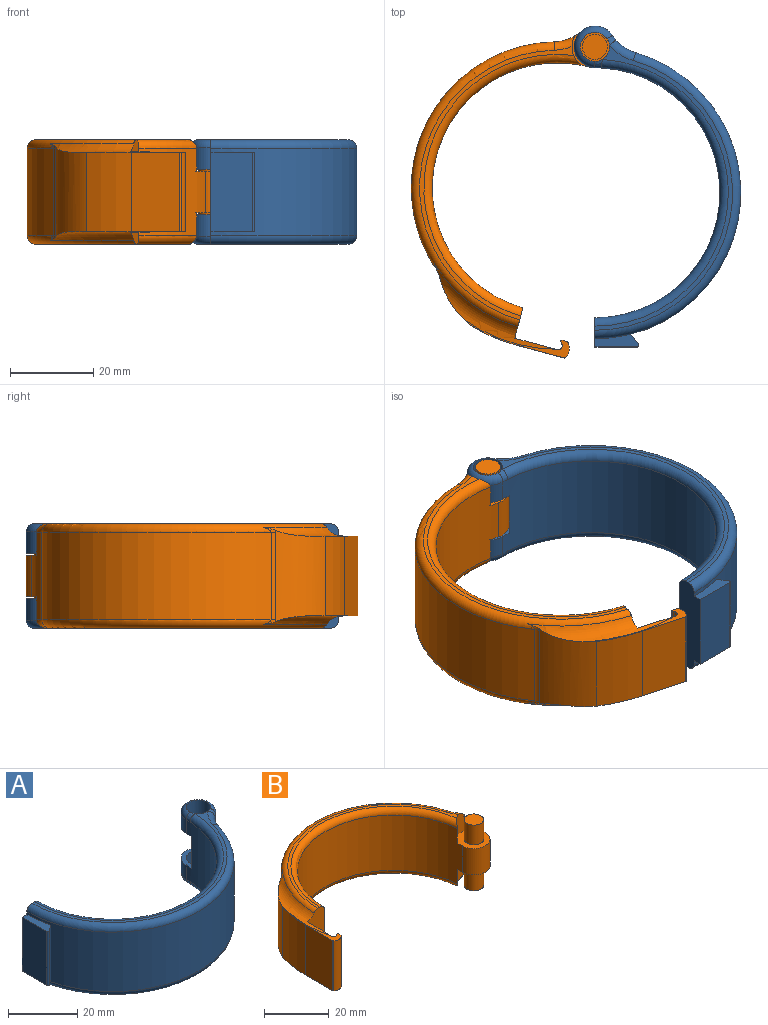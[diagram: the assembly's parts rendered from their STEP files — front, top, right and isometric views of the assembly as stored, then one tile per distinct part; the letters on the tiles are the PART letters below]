
ASSEMBLY  parts=2 mates=1
PART A: 30 faces, bbox 78.3x43.3x25.4 mm
  f0: cylinder r=35mm len=68.61mm, axis (0,0,-1), area 1936mm2, adj f4,f12,f13,f22,f27,f28,f29
  f1: cylinder r=3.5mm len=7mm, axis (0,0,-1), area 153.9mm2, adj f5,f11,f15,f16,f17
  f2: cylinder r=5mm len=10mm, axis (0,0,-1), area 104.6mm2, adj f3,f11,f12,f16
  f3: cylinder r=30mm len=60mm, axis (0,0,-1), area 1956mm2, adj f2,f4,f8,f9,f10,f11,f17,f18
  f4: plane 25x7mm, normal (0,1,0), area 159.6mm2, adj f0,f3,f5,f6,f13,f18,f19,f22
  f5: plane 68.36x33mm, normal (0,0,-1), area 104.8mm2, adj f1,f4,f13,f14,f18
  f6: plane 68.36x33mm, normal (0,0,1), area 104.8mm2, adj f4,f7,f19,f22,f24
  f7: cylinder r=3.5mm len=7mm, axis (0,0,-1), area 153.9mm2, adj f6,f10,f20,f21,f23
  f8: cylinder r=5mm len=10mm, axis (0,0,-1), area 104.6mm2, adj f3,f10,f12,f21
  f9: cylinder r=5.5mm len=11mm, axis (0,0,-1), area 85.3mm2, adj f3,f10,f11,f12
  f10: plane 10.5x10.08mm, normal (0,0,-1), area 44.4mm2, adj f3,f7,f8,f9,f12
  f11: plane 10.5x10.08mm, normal (0,0,1), area 44.4mm2, adj f1,f2,f3,f9,f12
  f12: cylinder r=10mm len=21.13mm, axis (0,0,1), area 128.3mm2, adj f0,f2,f8,f9,f10,f11,f14,f15
  f13: torus R=33mm, axis (0,0,1), area 307.8mm2, adj f0,f4,f5,f14
  f14: torus R=12mm, axis (0,0,1), area 19.3mm2, adj f5,f12,f13,f15
  f15: bspline ~2.98x2.54mm, area 4mm2, adj f1,f12,f14,f16
  f16: torus R=3mm, axis (0,0,-1), area 48.7mm2, adj f1,f2,f15,f17
  f17: bspline ~2.48x2.22mm, area 4.6mm2, adj f1,f3,f16,f18
  f18: torus R=32mm, axis (0,0,1), area 298.1mm2, adj f3,f4,f5,f17
  f19: torus R=32mm, axis (0,0,1), area 298.1mm2, adj f3,f4,f6,f20
  f20: bspline ~2.48x2.22mm, area 4.6mm2, adj f3,f7,f19,f21
  f21: torus R=3mm, axis (0,0,1), area 48.7mm2, adj f7,f8,f20,f23
  f22: torus R=33mm, axis (0,0,1), area 307.8mm2, adj f0,f4,f6,f24
  f23: bspline ~2.98x2.54mm, area 4mm2, adj f7,f12,f21,f24
  f24: torus R=12mm, axis (0,0,1), area 19.3mm2, adj f6,f12,f22,f23
  f25: plane 19x10mm, normal (-1,0,0), area 190mm2, adj f4,f26,f28,f29
  f26: cylinder r=0.5mm len=19mm, axis (0,0,-1), area 21.2mm2, adj f25,f27,f28,f29
  f27: plane 19x2.27mm, normal (0.62,-0.79,0), area 54.8mm2, adj f0,f26,f28,f29
  f28: plane 10.5x3.08mm, normal (0,0,1), area 23.8mm2, adj f0,f4,f25,f26,f27
  f29: plane 10.5x3.08mm, normal (0,0,-1), area 23.8mm2, adj f0,f4,f25,f26,f27
PART B: 41 faces, bbox 85.8x50.8x29 mm
  f0: cylinder r=35mm len=60.33mm, axis (0,0,-1), area 1585.1mm2, adj f14,f15,f17,f39
  f1: cylinder r=30mm len=60mm, axis (0,0,-1), area 1945.4mm2, adj f2,f3,f4,f7,f8,f11,f19,f20
  f2: plane 10.5x10.08mm, normal (0,0,1), area 54.6mm2, adj f1,f4,f9,f11,f14
  f3: plane 10.5x10.08mm, normal (0,0,-1), area 54.6mm2, adj f1,f7,f11,f13,f14
  f4: cylinder r=5.5mm len=7.5mm, axis (0,0,-1), area 52.5mm2, adj f1,f2,f5,f14,f16,f20
  f5: plane 66.63x32.5mm, normal (0,0,1), area 98.4mm2, adj f4,f8,f15,f16,f20
  f6: plane 66.63x32.5mm, normal (0,0,-1), area 98.4mm2, adj f7,f8,f17,f18,f19
  f7: cylinder r=5.5mm len=7.5mm, axis (0,0,-1), area 52.5mm2, adj f1,f3,f6,f14,f18,f19
  f8: plane 25.02x7.52mm, normal (0,-1,0), area 173mm2, adj f1,f5,f6,f15,f17,f19,f20,f30
  f9: cylinder r=3mm len=7.5mm, axis (0,0,-1), area 141.4mm2, adj f2,f10
  f10: plane 6x6mm, normal (0,0,1), area 28.3mm2, adj f9
  f11: cylinder r=5mm len=10mm, axis (0,0,-1), area 206.6mm2, adj f1,f2,f3,f14
  f12: plane 6x6mm, normal (0,0,-1), area 28.3mm2, adj f13
  f13: cylinder r=3mm len=7.5mm, axis (0,0,-1), area 141.4mm2, adj f3,f12
  f14: cylinder r=10mm len=21mm, axis (0,0,1), area 128.2mm2, adj f0,f2,f3,f4,f7,f11,f16,f18
  f15: torus R=33mm, axis (0,0,1), area 275.9mm2, adj f0,f5,f8,f16,f37,f40
  f16: torus R=12mm, axis (0,0,1), area 14.8mm2, adj f4,f5,f14,f15
  f17: torus R=33mm, axis (0,0,1), area 275.9mm2, adj f0,f6,f8,f18,f36,f38
  f18: torus R=12mm, axis (0,0,1), area 14.8mm2, adj f6,f7,f14,f17
  f19: torus R=32mm, axis (0,0,1), area 291.6mm2, adj f1,f6,f7,f8
  f20: torus R=32mm, axis (0,0,1), area 291.6mm2, adj f1,f4,f5,f8
  f21: cylinder r=0.35mm len=19mm, axis (0,0,-1), area 6.6mm2, adj f22,f33,f34,f35
  f22: plane 19x0.03mm, normal (-0.54,-0.84,0), area 0.7mm2, adj f21,f23,f34,f35
  f23: cylinder r=3.02mm len=19mm, axis (0,0,-1), area 71.2mm2, adj f22,f24,f34,f35
  f24: plane 19x0.12mm, normal (0.62,-0.79,0), area 2.8mm2, adj f23,f25,f34,f35
  f25: cylinder r=0.49mm len=19mm, axis (0,0,-1), area 8.4mm2, adj f24,f26,f34,f35
  f26: plane 19x1.19mm, normal (1,0,0), area 22.6mm2, adj f25,f27,f34,f35
  f27: cylinder r=0.23mm len=19mm, axis (0,0,-1), area 9.8mm2, adj f26,f28,f34,f35
  f28: plane 19x0.51mm, normal (-0.62,0.79,0), area 12.3mm2, adj f27,f29,f34,f35
  f29: cylinder r=1mm len=19mm, axis (0,0,-1), area 42.5mm2, adj f28,f30,f34,f35
  f30: plane 19.32x10.5mm, normal (1,0,0), area 201.3mm2, adj f8,f29,f34,f35,f36,f37
  f31: cylinder r=20.98mm len=21.9mm, axis (0,0,-1), area 282.1mm2, adj f32,f34,f35,f36,f37,f38,f39,f40
  f32: cylinder r=39mm len=19mm, axis (0,0,-1), area 223mm2, adj f31,f33,f34,f35
  f33: plane 19x12.08mm, normal (-1,0,0), area 229.6mm2, adj f21,f32,f34,f35
  f34: plane 26.24x4mm, normal (0,0,1), area 18.9mm2, adj f21,f22,f23,f24,f25,f26,f27,f28
  f35: plane 26.24x4mm, normal (0,0,-1), area 18.9mm2, adj f21,f22,f23,f24,f25,f26,f27,f28
  f36: torus R=38.74mm, axis (0,0,1), area 102.3mm2, adj f8,f17,f30,f31,f35,f38
  f37: torus R=38.74mm, axis (0,0,1), area 102.3mm2, adj f8,f15,f30,f31,f34,f40
  f38: bspline ~3.28x2.8mm, area 1.2mm2, adj f17,f31,f36,f39
  f39: cylinder r=3mm len=21mm, axis (0,0,1), area 24.6mm2, adj f0,f31,f38,f40
  f40: bspline ~3.28x2.8mm, area 1.2mm2, adj f15,f31,f37,f39
PLACE A rot(axis=(0,0,1),90deg) t=(46,-33.2,0)mm
PLACE B rot(axis=(0,0,1),75deg) t=(36.94,-32.01,0)mm
MATE revolute B.f4 <-> A.f1  axis (0,0,1) through (46,1.8,25)mm
